# Revit family: Timber Panel
name_source: partatom
category: Generic Models
revit_build: Autodesk Revit 2013 (Build: 20120221_2030(x64)
units: mm (PartAtom-declared; Revit-internal decimal feet)

## types (1)
- Timber Panel
    Bottom of Timber = -740 mm  [stored -2.42782 ft]
    Default Elevation = 1219 mm
    Distance from Centre = 50 mm  [stored 0.164042 ft]
    Frame Height = 1500 mm  [stored 4.92126 ft]
    Frame Material = Aluminum
    Frame Width = 2000 mm  [stored 6.56168 ft]
    Number of Planks = 7
    Runner Width = 50 mm  [stored 0.164042 ft]
    Slat Material = Douglas Fir
    Timber Depth = 50 mm  [stored 0.164042 ft]
    Timber Spacing = 100 mm  [stored 0.328084 ft]
    Timber Width = 50 mm  [stored 0.164042 ft]
    Top of Timber = 740 mm  [stored 2.42782 ft]

note: [stored X ft] marks values corroborated as IEEE doubles in the binary element streams (Revit-internal decimal feet)

## geometry (parser evidence)
native form markers: Blend x16, Sweep x2
no freeform markers — native parametric forms only
